# Revit family: NLRS_33_GM_FB_TC_STORAX_vloerluik_BV-F90_BCB
name_source: partatom
category: Generic Models
revit_build: Autodesk Revit 2014 (Build: 20130308_1515(x64)
units: mm (PartAtom-declared; Revit-internal decimal feet)

## types (10) — shared parameters
Manufacturer = Storax
Model = BV
URL = http://www.storax.nl
belasting = 125 kN
binnenluik = tbv betonvulling
brandwerend 90 min = ja
gasdrukveer = nee
geïsoleerd = ja
materiaal = bcb_staal
productgroep = Vloerluiken
rubberen_afdichting = enkel
scharnierend = nee
sluiting = 4
vergrendeling = nee
vullen_met_beton = ja
zero-valued in all types: Default Elevation

## per-type parameters (varying)
| type | binnenmaat_breedte | binnenmaat_lengte | gewicht | uitwendige_breedte | uitwendige_lengte |
| BV-F90 33 | 300 mm | 300 mm | 13 | 435 mm | 435 mm |
| BV-F90 45 | 450 mm | 450 mm | 21 | 585 mm | 585 mm |
| BV-F90 55 | 550 mm | 550 mm | 23 | 685 mm | 685 mm |
| BV-F90 64 | 400 mm  [stored 1.31234 ft] | 600 mm | 23 | 535 mm | 735 mm |
| BV-F90 66 | 600 mm | 600 mm | 30 | 735 mm | 735 mm |
| BV-F90 86 | 600 mm | 800 mm | 38 | 735 mm | 935 mm  [stored 3.06759 ft] |
| BV-F90 88 | 800 mm | 800 mm | 45 | 935 mm  [stored 3.06759 ft] | 935 mm  [stored 3.06759 ft] |
| BV-F90 106 | 600 mm | 1000 mm  [stored 3.28084 ft] | 45 | 735 mm | 1135 mm  [stored 3.72375 ft] |
| BV-F90 108 | 800 mm | 1000 mm  [stored 3.28084 ft] | 54 | 935 mm  [stored 3.06759 ft] | 1135 mm  [stored 3.72375 ft] |
| BV-F90 110 | 1000 mm  [stored 3.28084 ft] | 1000 mm  [stored 3.28084 ft] | 63 | 1135 mm  [stored 3.72375 ft] | 1135 mm  [stored 3.72375 ft] |

note: [stored X ft] marks values corroborated as IEEE doubles in the binary element streams (Revit-internal decimal feet)

## geometry (parser evidence)
native form markers: Blend x811, Sweep x4
no freeform markers — native parametric forms only
